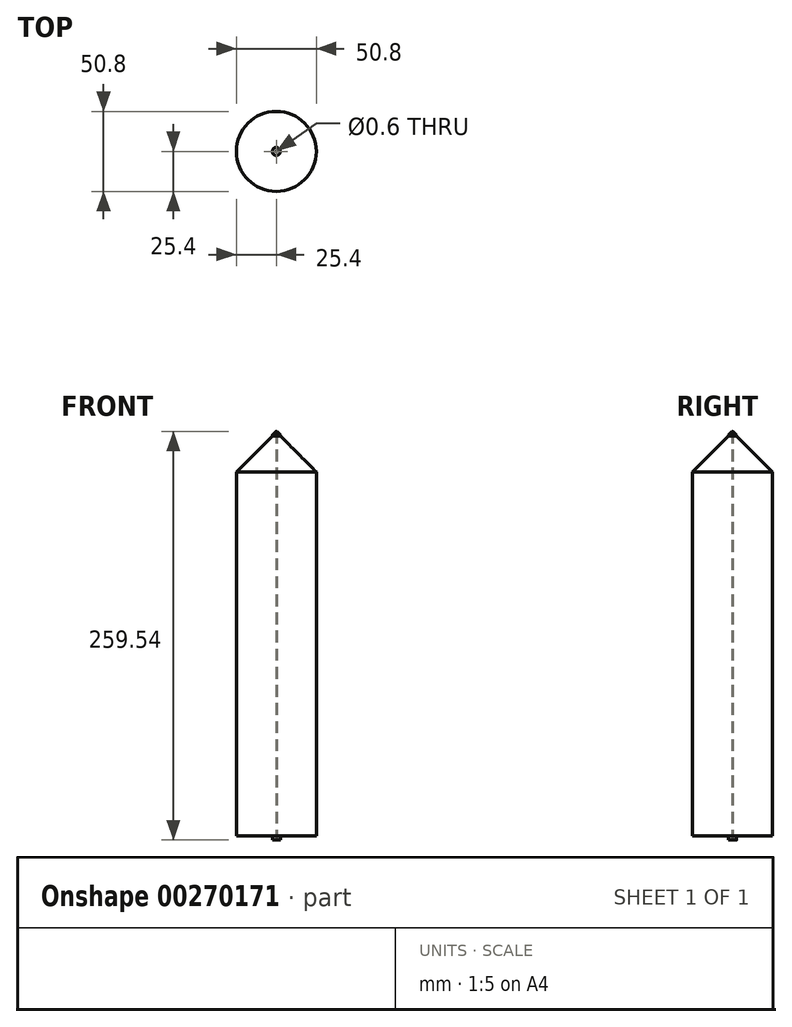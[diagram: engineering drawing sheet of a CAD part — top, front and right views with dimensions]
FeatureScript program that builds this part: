
annotation { "Feature Type Name" : "Feature", "Feature Type Description" : "" }
export const myFeature = defineFeature(function(context is Context, id is Id, definition is map)
    precondition{}
    {
        {
            var Q0;
            Q0=qCreatedBy(makeId("Top.planeOp"),FACE);
            var sketch = newSketch(context, id + "F0", { "sketchPlane" : qUnion([Q0])});
            skCircle(sketch, "E0", {"center": v(0, 0) * mm, "radius": 25.4 * mm});
            skSolve(sketch);
        }
        {
            var Q0;
            Q0 = qSketchRegion(id + "F0", true);
            extrude(context, id + "F1", {"entities" : qUnion([Q0]), "endBound" : BoundingType.SYMMETRIC, "depth" : 254 * mm});
        }
        {
            var Q0;
            Q0=makeQuery(id+"F1.opExtrude","CAP_FACE",FACE,{"disambiguationData":[OSD([sQuery(id+"F0.wireOp",EDGE,"E0")])],"isStart":false});
            chamfer(context, id + "F2", {"entities" : qUnion([Q0]), "width" : 22.86 * mm, "tangentPropagation" : true});
        }
        {
            var Q0;
            Q0=qCreatedBy(makeId("Top.planeOp"),FACE);
            var sketch = newSketch(context, id + "F3", { "sketchPlane" : qUnion([Q0])});
            skSolve(sketch);
        }
        {
            var Q0;
            Q0 = qSketchRegion(id + "F3", true);
            var Q1;
            Q1=makeQuery(id+"F1.opExtrude","CAP_FACE",FACE,{"disambiguationData":[OSD([sQuery(id+"F0.wireOp",EDGE,"E0")])],"isStart":false});
            extrude(context, id + "F4", {"entities" : qUnion([Q0, Q1]), "operationType" : NewBodyOperationType.REMOVE, "endBound" : BoundingType.THROUGH_ALL, "oppositeDirection" : true, "depth" : 25.4 * mm});
        }
        {
            var Q0;
            Q0=qCreatedBy(makeId("Top.planeOp"),FACE);
            var sketch = newSketch(context, id + "F5", { "sketchPlane" : qUnion([Q0])});
            skCircle(sketch, "E1", {"center": v(0, 0) * mm, "radius": 0.3 * mm});
            skCircle(sketch, "E2", {"center": v(0, 0) * mm, "radius": 2.54 * mm});
            skSolve(sketch);
        }
        {
            var Q0;
            Q0=makeQuery(id+"F5.imprint","IMPRINT",FACE,{"disambiguationData":[TD([[makeQuery(id+"F5.imprint","IMPRINT",EDGE,{"derivedFrom":sQuery(id+"F5.wireOp",EDGE,"E1")}),-1.0]])]});
            extrude(context, id + "F6", {"entities" : qUnion([Q0]), "operationType" : NewBodyOperationType.ADD, "endBound" : BoundingType.SYMMETRIC, "depth" : 259.59 * mm});
        }
        {
            var Q0;
            Q0=makeQuery(id+"F6.opExtrude","CAP_EDGE",EDGE,{"disambiguationData":[OSD([sQuery(id+"F5.wireOp",EDGE,"E2")])],"isStart":false});
            chamfer(context, id + "F7", {"entities" : qUnion([Q0]), "width" : 2.3 * mm, "tangentPropagation" : true});
        }
    });
